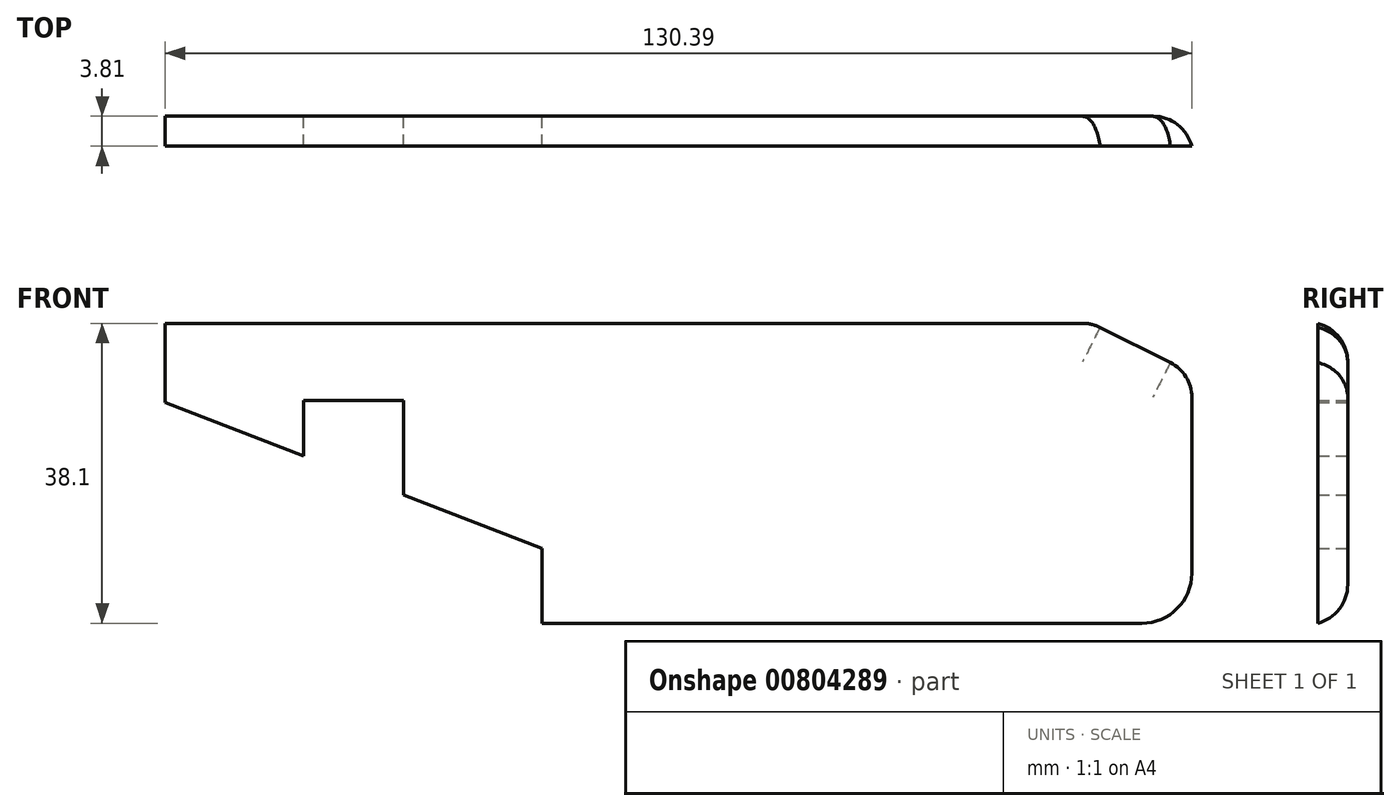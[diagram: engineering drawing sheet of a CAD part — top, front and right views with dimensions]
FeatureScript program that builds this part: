
annotation { "Feature Type Name" : "Feature", "Feature Type Description" : "" }
export const myFeature = defineFeature(function(context is Context, id is Id, definition is map)
    precondition{}
    {
        {
            var Q0;
            Q0=qCreatedBy(makeId("Front.planeOp"),FACE);
            var sketch = newSketch(context, id + "F0", { "sketchPlane" : qUnion([Q0])});
            skLineSegment(sketch, "E0.MirrorCS", {"start": v(95.25, 38.1) * mm, "end": v(0, 38.1) * mm});
            skLineSegment(sketch, "E1.MirrorCS", {"start": v(50.8, 0) * mm, "end": v(101.6, 0) * mm});
            skLineSegment(sketch, "E2.MirrorCS", {"start": v(107.95, 6.35) * mm, "end": v(107.95, 31.75) * mm});
            skLineSegment(sketch, "E3.MirrorCS", {"start": v(107.95, 31.75) * mm, "end": v(95.25, 38.1) * mm});
            skArc(sketch, "E4.MirrorCS", {"start": v(107.95, 6.35) * mm, "mid": v(106.1, 1.86) * mm, "end": v(101.6, 0) * mm});
            skLineSegment(sketch, "E5", {"start": v(-22.44, 38.1) * mm, "end": v(0, 38.1) * mm});
            skPoint(sketch, "E6.orphan", {"position": v(0, 0) * mm});
            skLineSegment(sketch, "E7", {"start": v(50.8, 0) * mm, "end": v(25.4, 0) * mm});
            skLineSegment(sketch, "E8", {"start": v(25.4, 9.52) * mm, "end": v(25.4, 0) * mm});
            skLineSegment(sketch, "E9", {"start": v(-22.44, 28.03) * mm, "end": v(-22.44, 38.1) * mm});
            skLineSegment(sketch, "E10", {"start": v(-22.44, 28.03) * mm, "end": v(-4.87, 21.23) * mm});
            skLineSegment(sketch, "E11", {"start": v(-4.87, 28.3) * mm, "end": v(-4.87, 21.23) * mm});
            skLineSegment(sketch, "E12", {"start": v(7.83, 28.3) * mm, "end": v(7.83, 16.32) * mm});
            skLineSegment(sketch, "E13", {"start": v(-4.87, 28.3) * mm, "end": v(7.83, 28.3) * mm});
            skLineSegment(sketch, "E14.trimOffspring", {"start": v(7.83, 16.32) * mm, "end": v(25.4, 9.52) * mm});
            skSolve(sketch);
        }
        {
            var Q0;
            Q0=makeQuery(id+"F0.imprint","IMPRINT",FACE,{"disambiguationData":[TD([[makeQuery(id+"F0.imprint","IMPRINT",EDGE,{"derivedFrom":sQuery(id+"F0.wireOp",EDGE,"02fd4ccf-6958-43b7-ac44-ca74b49f6ff0")}),1.0]])]});
            var Q1;
            Q1=makeQuery(id+"F0.imprint","IMPRINT",FACE,{"disambiguationData":[TD([[makeQuery(id+"F0.imprint","IMPRINT",EDGE,{"derivedFrom":sQuery(id+"F0.wireOp",EDGE,"02fd4ccf-6958-43b7-ac44-ca74b49f6ff0")}),-1.0]])]});
            var Q2;
            Q2=makeQuery(id+"F0.imprint","IMPRINT",FACE,{"disambiguationData":[TD([[makeQuery(id+"F0.imprint","IMPRINT",EDGE,{"derivedFrom":sQuery(id+"F0.wireOp",EDGE,"E0.MirrorCS")}),1.0]])]});
            extrude(context, id + "F1", {"entities" : qUnion([Q0, Q1, Q2]), "depth" : 3.8 * mm, "offsetDistance" : 25.4 * mm});
        }
        {
            var Q0;
            Q0=makeQuery(id+"F1.opExtrude","CAP_EDGE",EDGE,{"disambiguationData":[OSD([sQuery(id+"F0.wireOp",EDGE,"E1.MirrorCS")])],"isStart":true});
            var Q1;
            Q1=makeQuery(id+"F1.opExtrude","CAP_EDGE",EDGE,{"disambiguationData":[OSD([sQuery(id+"F0.wireOp",EDGE,"E4.MirrorCS")])],"isStart":true});
            var Q2;
            Q2=makeQuery(id+"F1.opExtrude","CAP_EDGE",EDGE,{"disambiguationData":[OSD([sQuery(id+"F0.wireOp",EDGE,"E2.MirrorCS")])],"isStart":true});
            var Q3;
            Q3=makeQuery(id+"F1.opExtrude","CAP_EDGE",EDGE,{"disambiguationData":[OSD([sQuery(id+"F0.wireOp",EDGE,"E0.MirrorCS"),sQuery(id+"F0.wireOp",EDGE,"E5")])],"isStart":true});
            var Q4;
            Q4=makeQuery(id+"F1.opExtrude","CAP_EDGE",EDGE,{"disambiguationData":[OSD([sQuery(id+"F0.wireOp",EDGE,"E3.MirrorCS")])],"isStart":true});
            fillet(context, id + "F2", {"entities" : qUnion([Q0, Q1, Q2, Q3, Q4]), "radius" : 5.08 * mm, "tangentPropagation" : true, "allowEdgeOverflow" : false});
        }
        {
            var Q0;
            Q0=makeQuery(id+"F2.opFillet","BLEND_EDGE",EDGE,{"blendedFrom":[makeQuery(id+"F1.opExtrude","CAP_EDGE",EDGE,{"disambiguationData":[OSD([sQuery(id+"F0.wireOp",EDGE,"E2.MirrorCS")])],"isStart":true}),makeQuery(id+"F1.opExtrude","CAP_EDGE",EDGE,{"disambiguationData":[OSD([sQuery(id+"F0.wireOp",EDGE,"E3.MirrorCS")])],"isStart":true})],"blendedInto":[]});
            var Q1;
            Q1=makeQuery(id+"F2.opFillet","BLEND_EDGE",EDGE,{"blendedFrom":[makeQuery(id+"F1.opExtrude","CAP_EDGE",EDGE,{"disambiguationData":[OSD([sQuery(id+"F0.wireOp",EDGE,"E0.MirrorCS"),sQuery(id+"F0.wireOp",EDGE,"E5")])],"isStart":true}),makeQuery(id+"F1.opExtrude","CAP_EDGE",EDGE,{"disambiguationData":[OSD([sQuery(id+"F0.wireOp",EDGE,"E3.MirrorCS")])],"isStart":true})],"blendedInto":[]});
            fillet(context, id + "F3", {"entities" : qUnion([Q0, Q1]), "radius" : 5.08 * mm, "tangentPropagation" : true, "allowEdgeOverflow" : false});
        }
    });
